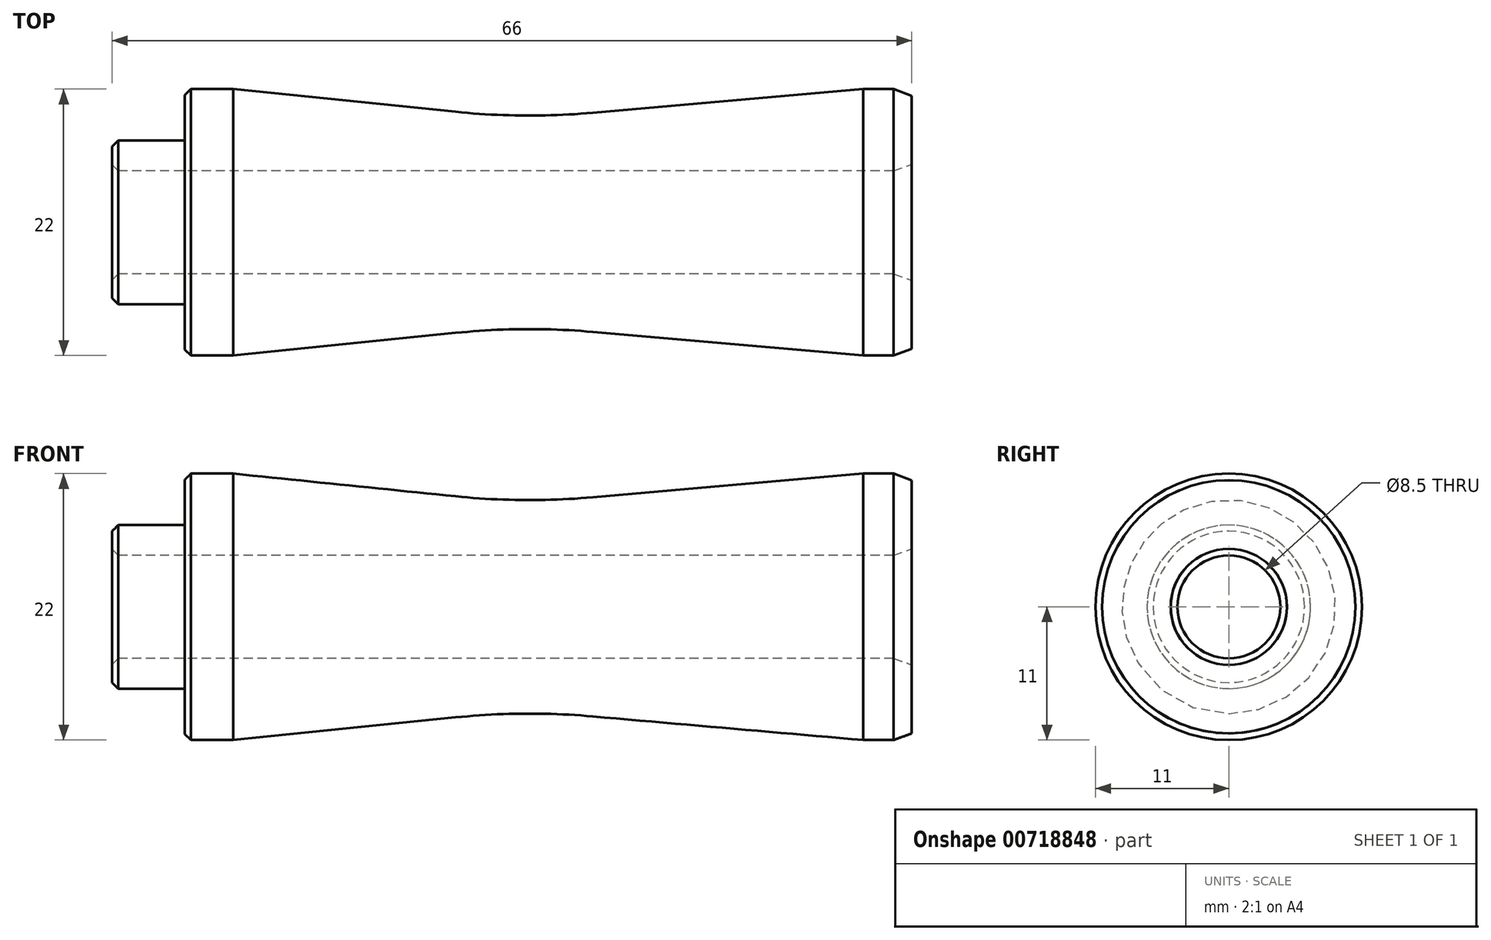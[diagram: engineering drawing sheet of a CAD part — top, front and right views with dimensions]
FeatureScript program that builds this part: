
annotation { "Feature Type Name" : "Feature", "Feature Type Description" : "" }
export const myFeature = defineFeature(function(context is Context, id is Id, definition is map)
    precondition{}
    {
        {
            var Q0;
            Q0=qCreatedBy(makeId("Right.planeOp"),FACE);
            var sketch = newSketch(context, id + "F0", { "sketchPlane" : qUnion([Q0])});
            skCircle(sketch, "E0", {"center": v(0, 0) * mm, "radius": 4.25 * mm});
            skCircle(sketch, "E1", {"center": v(0, 0) * mm, "radius": 11 * mm});
            skSolve(sketch);
        }
        {
            var Q0;
            Q0=makeQuery(id+"F0.imprint","IMPRINT",FACE,{"disambiguationData":[TD([[makeQuery(id+"F0.imprint","IMPRINT",EDGE,{"derivedFrom":sQuery(id+"F0.wireOp",EDGE,"E0")}),-1.0]])]});
            extrude(context, id + "F1", {"entities" : qUnion([Q0]), "depth" : 2 * mm, "offsetDistance" : 25 * mm});
        }
        {
            var Q0;
            Q0=makeQuery(id+"F1.opExtrude","CAP_FACE",FACE,{"disambiguationData":[OSD([sQuery(id+"F0.wireOp",EDGE,"E0"),sQuery(id+"F0.wireOp",EDGE,"bd1b2cdd-5617-4c78-8d76-927c4d231982.0"),sQuery(id+"F0.wireOp",EDGE,"bd1b2cdd-5617-4c78-8d76-927c4d231982.1"),sQuery(id+"F0.wireOp",EDGE,"bd1b2cdd-5617-4c78-8d76-927c4d231982.2"),sQuery(id+"F0.wireOp",EDGE,"bd1b2cdd-5617-4c78-8d76-927c4d231982.3"),sQuery(id+"F0.wireOp",EDGE,"bd1b2cdd-5617-4c78-8d76-927c4d231982.4"),sQuery(id+"F0.wireOp",EDGE,"bd1b2cdd-5617-4c78-8d76-927c4d231982.5")])],"isStart":false});
            var sketch = newSketch(context, id + "F2", { "sketchPlane" : qUnion([Q0])});
            skCircle(sketch, "E2", {"center": v(0, 0) * mm, "radius": 11 * mm});
            skCircle(sketch, "E3", {"center": v(0, 0) * mm, "radius": 4.25 * mm});
            skSolve(sketch);
        }
        {
            var Q0;
            Q0=makeQuery(id+"F2.imprint","IMPRINT",FACE,{"disambiguationData":[TD([[makeQuery(id+"F2.imprint","IMPRINT",EDGE,{"derivedFrom":sQuery(id+"F2.wireOp",EDGE,"E3")}),-1.0]])]});
            var Q1;
            {var subQ2=sQuery(id+"F0.wireOp",EDGE,"bd1b2cdd-5617-4c78-8d76-927c4d231982.3");var subQ9=makeQuery(id+"F1.opExtrude","CAP_EDGE",EDGE,{"disambiguationData":[OSD([subQ2])],"isStart":false});Q1=makeQuery(id+"F2.imprint","IMPRINT",FACE,{"disambiguationData":[TD([[makeQuery(id+"F2.imprint","IMPRINT",EDGE,{"derivedFrom":subQ9}),1.0]])]});}
            var Q2;
            {var subQ2=sQuery(id+"F0.wireOp",EDGE,"bd1b2cdd-5617-4c78-8d76-927c4d231982.4");var subQ9=makeQuery(id+"F1.opExtrude","CAP_EDGE",EDGE,{"disambiguationData":[OSD([subQ2])],"isStart":false});Q2=makeQuery(id+"F2.imprint","IMPRINT",FACE,{"disambiguationData":[TD([[makeQuery(id+"F2.imprint","IMPRINT",EDGE,{"derivedFrom":subQ9}),1.0]])]});}
            var Q3;
            {var subQ2=sQuery(id+"F0.wireOp",EDGE,"bd1b2cdd-5617-4c78-8d76-927c4d231982.2");var subQ9=makeQuery(id+"F1.opExtrude","CAP_EDGE",EDGE,{"disambiguationData":[OSD([subQ2])],"isStart":false});Q3=makeQuery(id+"F2.imprint","IMPRINT",FACE,{"disambiguationData":[TD([[makeQuery(id+"F2.imprint","IMPRINT",EDGE,{"derivedFrom":subQ9}),1.0]])]});}
            var Q4;
            {var subQ2=sQuery(id+"F0.wireOp",EDGE,"bd1b2cdd-5617-4c78-8d76-927c4d231982.1");var subQ9=makeQuery(id+"F1.opExtrude","CAP_EDGE",EDGE,{"disambiguationData":[OSD([subQ2])],"isStart":false});Q4=makeQuery(id+"F2.imprint","IMPRINT",FACE,{"disambiguationData":[TD([[makeQuery(id+"F2.imprint","IMPRINT",EDGE,{"derivedFrom":subQ9}),1.0]])]});}
            var Q5;
            {var subQ3=sQuery(id+"F0.wireOp",EDGE,"bd1b2cdd-5617-4c78-8d76-927c4d231982.0");var subQ9=makeQuery(id+"F1.opExtrude","CAP_EDGE",EDGE,{"disambiguationData":[OSD([subQ3])],"isStart":false});Q5=makeQuery(id+"F2.imprint","IMPRINT",FACE,{"disambiguationData":[TD([[makeQuery(id+"F2.imprint","IMPRINT",EDGE,{"derivedFrom":subQ9}),1.0]])]});}
            var Q6;
            {var subQ1=sQuery(id+"F0.wireOp",EDGE,"bd1b2cdd-5617-4c78-8d76-927c4d231982.5");var subQ9=makeQuery(id+"F1.opExtrude","CAP_EDGE",EDGE,{"disambiguationData":[OSD([subQ1])],"isStart":false});Q6=makeQuery(id+"F2.imprint","IMPRINT",FACE,{"disambiguationData":[TD([[makeQuery(id+"F2.imprint","IMPRINT",EDGE,{"derivedFrom":subQ9}),1.0]])]});}
            extrude(context, id + "F3", {"entities" : qUnion([Q0, Q1, Q2, Q3, Q4, Q5, Q6]), "operationType" : NewBodyOperationType.ADD, "depth" : 2 * mm, "offsetDistance" : 25 * mm});
        }
        {
            var Q0;
            Q0=qCreatedBy(makeId("Top.planeOp"),FACE);
            var sketch = newSketch(context, id + "F4", { "sketchPlane" : qUnion([Q0])});
            skLineSegment(sketch, "E4", {"start": v(7.32, 0) * mm, "end": v(-69.26, 0) * mm});
            skSolve(sketch);
        }
        {
            var Q0;
            Q0=qCreatedBy(makeId("Front.planeOp"),FACE);
            var sketch = newSketch(context, id + "F5", { "sketchPlane" : qUnion([Q0])});
            skLineSegment(sketch, "E5.bottom", {"start": v(-52, 11) * mm, "end": v(-56, 11) * mm});
            skLineSegment(sketch, "E5.right", {"start": v(-56, 11) * mm, "end": v(-56, 6.75) * mm});
            skLineSegment(sketch, "E6", {"start": v(0, 11) * mm, "end": v(-28, 8.55) * mm});
            skLineSegment(sketch, "E7", {"start": v(-28, 8.55) * mm, "end": v(-52, 11) * mm});
            skLineSegment(sketch, "E8", {"start": v(0, 4.25) * mm, "end": v(-62, 4.25) * mm});
            skLineSegment(sketch, "E9", {"start": v(0, 11) * mm, "end": v(0, 4.25) * mm});
            skLineSegment(sketch, "E10.bottom", {"start": v(-56, 6.75) * mm, "end": v(-62, 6.75) * mm});
            skLineSegment(sketch, "E10.right", {"start": v(-62, 6.75) * mm, "end": v(-62, 4.25) * mm});
            skSolve(sketch);
        }
        {
            var Q0;
            {var subQ1=sQuery(id+"F5.wireOp",EDGE,"E5.bottom");Q0=makeQuery(id+"F5.imprint","IMPRINT",FACE,{"disambiguationData":[TD([[makeQuery(id+"F5.imprint","IMPRINT",EDGE,{"derivedFrom":subQ1}),1.0]])]});}
            var Q1;
            {var subQ3=sQuery(id+"F5.wireOp",EDGE,"E10.bottom");Q1=makeQuery(id+"F5.imprint","IMPRINT",FACE,{"disambiguationData":[TD([[makeQuery(id+"F5.imprint","IMPRINT",EDGE,{"derivedFrom":subQ3}),1.0]])]});}
            var Q2;
            Q2=sQuery(id+"F4.wireOp",EDGE,"E4");
            revolve(context, id + "F6", {"operationType" : NewBodyOperationType.ADD, "surfaceOperationType" : NewSurfaceOperationType.NEW, "entities" : qUnion([Q0, Q1]), "axis" : qUnion([Q2]), "revolveType" : RevolveType.FULL});
        }
        {
            var Q0;
            Q0=makeQuery(id+"F6.opRevolve","SWEPT_EDGE",EDGE,{"disambiguationData":[OSD([sQuery(id+"F5.wireOp",EDGE,"E6"),sQuery(id+"F5.wireOp",EDGE,"E7")])]});
            fillet(context, id + "F7", {"entities" : qUnion([Q0]), "radius" : 60 * mm, "tangentPropagation" : true, "allowEdgeOverflow" : false});
        }
        {
            var Q0;
            Q0=makeQuery(id+"F6.opRevolve","SWEPT_EDGE",EDGE,{"disambiguationData":[OSD([sQuery(id+"F5.wireOp",EDGE,"E10.bottom"),sQuery(id+"F5.wireOp",EDGE,"E10.right")])]});
            var Q1;
            Q1=makeQuery(id+"F6.opRevolve","SWEPT_FACE",FACE,{"disambiguationData":[OSD([sQuery(id+"F5.wireOp",EDGE,"E10.right")])]});
            chamfer(context, id + "F8", {"entities" : qUnion([Q0, Q1]), "width" : 0.5 * mm, "tangentPropagation" : true});
        }
        {
            var Q0;
            Q0=makeQuery(id+"F6.opRevolve","SWEPT_EDGE",EDGE,{"disambiguationData":[OSD([sQuery(id+"F5.wireOp",EDGE,"E5.bottom"),sQuery(id+"F5.wireOp",EDGE,"E5.right")])]});
            chamfer(context, id + "F9", {"entities" : qUnion([Q0]), "width" : 0.5 * mm, "tangentPropagation" : true});
        }
        {
            var Q0;
            Q0=makeQuery(id+"F3.opExtrude","CAP_EDGE",EDGE,{"disambiguationData":[OSD([sQuery(id+"F2.wireOp",EDGE,"E2")])],"isStart":false});
            chamfer(context, id + "F10", {"entities" : qUnion([Q0]), "chamferType" : ChamferType.OFFSET_ANGLE, "width" : 1.5 * mm, "oppositeDirection" : true, "angle" : 20 * degree, "tangentPropagation" : true});
        }
        {
            var Q0;
            Q0=makeQuery(id+"F3.opExtrude","CAP_EDGE",EDGE,{"disambiguationData":[OSD([sQuery(id+"F2.wireOp",EDGE,"E3")])],"isStart":false});
            chamfer(context, id + "F11", {"entities" : qUnion([Q0]), "chamferType" : ChamferType.OFFSET_ANGLE, "width" : 1.5 * mm, "oppositeDirection" : false, "angle" : 20 * degree, "tangentPropagation" : true});
        }
    });
